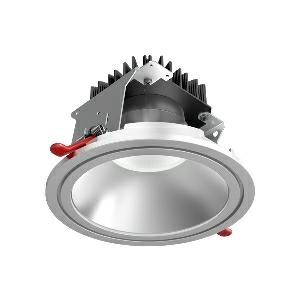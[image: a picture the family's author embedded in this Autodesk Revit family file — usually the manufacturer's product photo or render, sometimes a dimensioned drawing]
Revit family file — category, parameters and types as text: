
# Revit family: dotoo_spot_-_dse_1000_840_00806083_3413
name_source: partatom
category: Lighting Fixtures
units: mm (PartAtom-declared; Revit-internal decimal feet)

## family parameters
Cut with Voids When Loaded = No
Host = Face
Light Source = No
Part Type = Normal
Room Calculation Point = No
Round Connector Dimension = Use Diameter
Shared = No

## types (1)
- DOTOO.spot - DSE 1000/840 (1 x LED, 1400 lm, 4000K)
    Apparent Load = 14 VA
    Approval mark = CE
    CIE Flux Codes = 87 99 100 100 100
    Color Rendering = 80-89
    Color Temperature = 4000K
    Control Gear = Electronic ballast
    Default Elevation = 1800 mm
    Description = DSE 1000/840|Recessed luminaire|light source: LED|work equipment: Electronic ballast|connected load: 220-240 V, 50/60 Hz|Power consumption: approx. 14 W|standby: approx. 0,20|power factor: approx. 0,900|luminous flux: 1400 lm|luminous efficacy: 100 lm/W|light distribution: Direct|direct ratio: approx. 100 %|colour temperature: Cold white, ca. 4000 K|color rendering index (CRI): >= 80|chromaticity tolerance:  3 SDCM|System of protection: IP 20|class of protection: II|technology: Switchable|operation: External|luminaire body|material: Sheet metal|colour: White|weight (net): approx. 0.7 kg|mains lead: 0.35 m Connector|Fastening: Tension spring|glare control: Prism aperture|luminance(L65): <= 2100 cd/m|unified glare rating(4H 8H): <=  19|special features: Flicker-free, Low installation depth thanks to external ballast, Suitable as emergency lighting, Ceiling installation without tools by means of tension springs, Strain relief with the possibility of through-wiring, As supplement for room depths and walking areas|
    Height = 0 mm  [stored 0 ft]
    Lamp = 1 x LED
    Lamp Light Flux = 1400 lm
    Lamp count = 1
    Length = 166 mm
    Luminous efficacy = 100 lm/W
    Manufacturer = Waldmann
    ModVariant = No
    Model = 00806083
    Mounting Place = Ceiling
    Mounting Type = Recessed
    Number of Poles = 1
    OnlyDefault = Yes
    Power Factor = 1
    Product Name = DOTOO.spot - DSE 1000/840
    Product group = Recessed luminaire
    ProductGroupID = 4
    Protection Class = Protection class II
    Protection Degree = IP 20
    RLX_Detail_Level = 1
    RLX_Emergency_Light_Flux = 0 lm
    RLX_Emergency_Type = 0
    RLX_Emergency_Type_DB = No
    RlxData = <blob elided: 53869 chars, md5=2a23aaa5>
    Socket = socket
    Standby Power = 0 W
    System Light Flux = 1400 lm
    System Power = 14 W
    Type Comments = Product without accessories
    Type Image = 114272000-00806084.jpg
    URL = http://relux.com
    VarID = ---
    Voltage = 230 V
    Voltage Range = 220-240 V
    Weight = 0.00 kg
    Width = 0 mm  [stored 0 ft]

note: [stored X ft] marks values corroborated as IEEE doubles in the binary element streams (Revit-internal decimal feet)

## geometry (parser evidence)
native form markers: Blend x4, Sweep x12
no freeform markers — native parametric forms only
